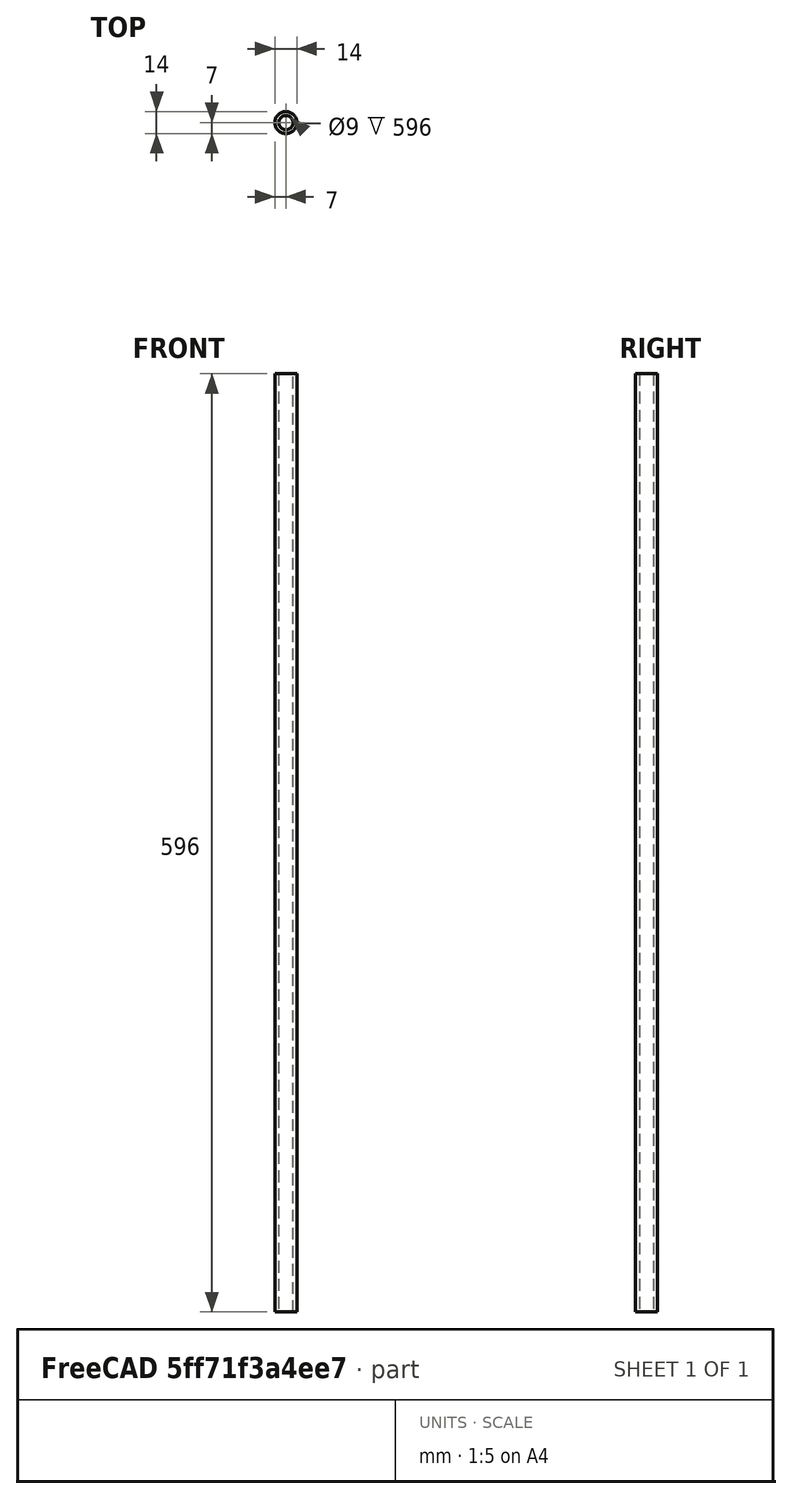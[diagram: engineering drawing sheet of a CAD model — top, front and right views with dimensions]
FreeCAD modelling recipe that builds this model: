
FCSTD DOCUMENT  (FreeCAD 1.0R39319 (Git))
Label: pcp_barel_14x2_5x596mm_9mmid
License: All rights reserved
LicenseURL: https://en.wikipedia.org/wiki/All_rights_reserved
objects: Sketcher::SketchObject×1, PartDesign::Pad×1, PartDesign::Body×1
note: 6 computed .brp shape members not serialized (recipe doc carries the construction recipe); baked Part::Feature solids carry a one-line shape summary decoded from their .brp

FEATURE [Sketcher::SketchObject] Sketch
  ArcFitTolerance = 1e-06
  AttachmentSupport = -> [XY_Plane]
  FullyConstrained = true
  MakeInternals = false
  MapMode = 5
  sketch-geometry (2):
    g0: Circle CenterX=0 CenterY=0 CenterZ=0 NormalX=0 NormalY=0 NormalZ=1 AngleXU=0 Radius=7
    g1: Circle CenterX=0 CenterY=0 CenterZ=0 NormalX=0 NormalY=0 NormalZ=1 AngleXU=0 Radius=4.5
  constraints (4):
    c: Diameter(g0) = 14
    c: Coincident(g0,g-1)
    c: Diameter(g1) = 9
    c: Coincident(g1,g0)
FEATURE [PartDesign::Pad] Pad
  Direction = (0,0,1)
  Length = 596
  Length2 = 10
  Profile = -> Sketch
  ReferenceAxis = -> Sketch [N_Axis]
  Refine = true
  Suppressed = false
  Type = 0
FEATURE [PartDesign::Body] Body
  AllowCompound = false
  Group = -> [Sketch,Pad]
  Origin = -> Origin
  Tip = -> Pad
